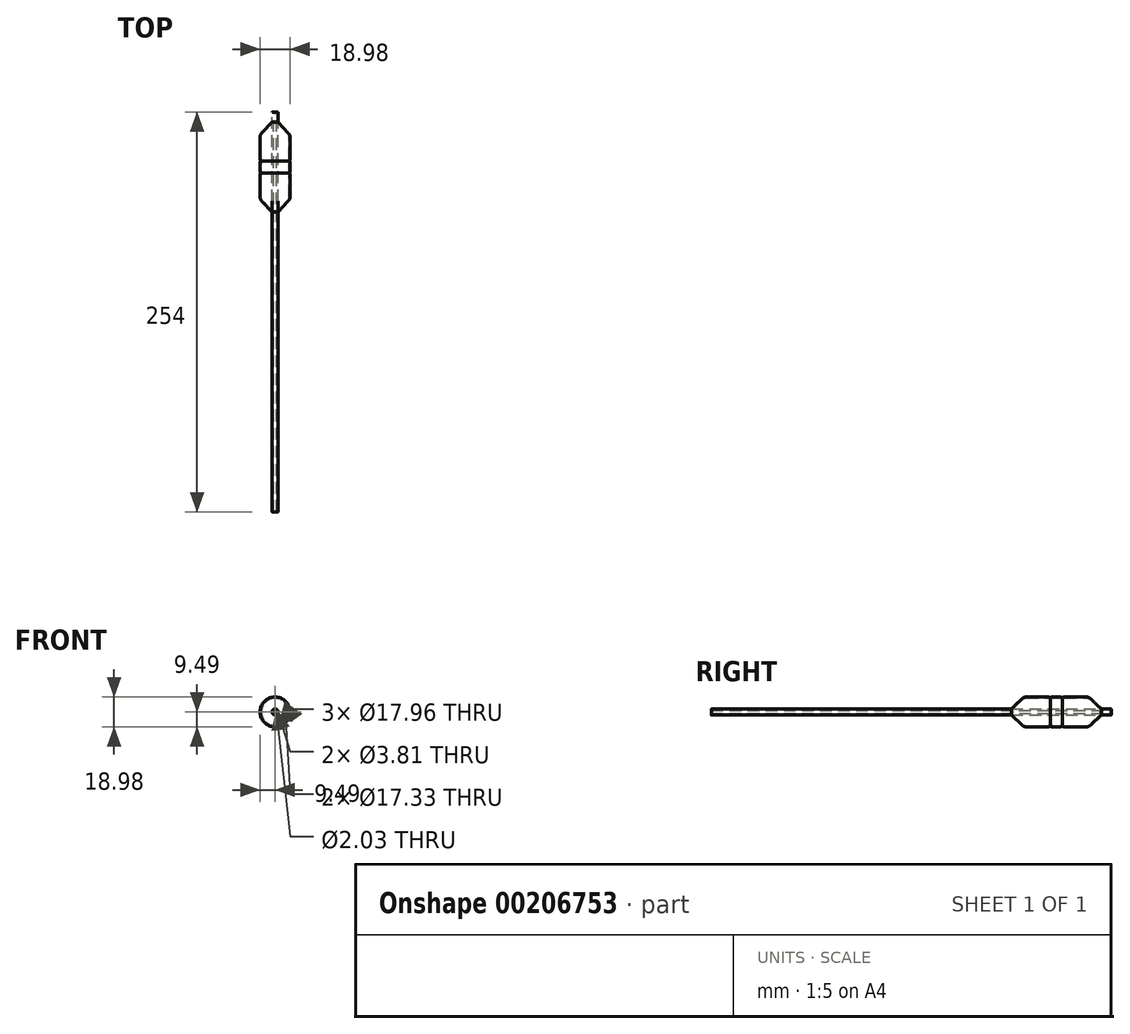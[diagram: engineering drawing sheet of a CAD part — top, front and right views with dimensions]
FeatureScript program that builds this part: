
annotation { "Feature Type Name" : "Feature", "Feature Type Description" : "" }
export const myFeature = defineFeature(function(context is Context, id is Id, definition is map)
    precondition{}
    {
        {
            var Q0;
            Q0=qCreatedBy(makeId("Front.planeOp"),FACE);
            var sketch = newSketch(context, id + "F0", { "sketchPlane" : qUnion([Q0])});
            skCircle(sketch, "E0", {"center": v(0, 0) * mm, "radius": 1.02 * mm});
            skCircle(sketch, "E1", {"center": v(0, 0) * mm, "radius": 1.9 * mm});
            skSolve(sketch);
        }
        {
            var Q0;
            Q0=makeQuery(id+"F0.imprint","IMPRINT",FACE,{"disambiguationData":[TD([[makeQuery(id+"F0.imprint","IMPRINT",EDGE,{"derivedFrom":sQuery(id+"F0.wireOp",EDGE,"E0")}),-1.0]])]});
            extrude(context, id + "F1", {"entities" : qUnion([Q0]), "depth" : 254 * mm});
        }
        {
            var Q0;
            Q0=makeQuery(id+"F1.opExtrude","CAP_EDGE",EDGE,{"disambiguationData":[OSD([sQuery(id+"F0.wireOp",EDGE,"E0")])],"isStart":true});
            chamfer(context, id + "F2", {"entities" : qUnion([Q0]), "width" : 0.56 * mm, "tangentPropagation" : true});
        }
        {
            var Q0;
            Q0=makeQuery(id+"F1.opExtrude","CAP_EDGE",EDGE,{"disambiguationData":[OSD([sQuery(id+"F0.wireOp",EDGE,"E1")])],"isStart":true});
            fillet(context, id + "F3", {"entities" : qUnion([Q0]), "radius" : 0.13 * mm, "tangentPropagation" : true, "allowEdgeOverflow" : false});
        }
        {
            var Q0;
            Q0=makeQuery(id+"F1.opExtrude","CAP_EDGE",EDGE,{"disambiguationData":[OSD([sQuery(id+"F0.wireOp",EDGE,"E1")])],"isStart":false});
            fillet(context, id + "F4", {"entities" : qUnion([Q0]), "radius" : 0.13 * mm, "tangentPropagation" : true, "allowEdgeOverflow" : false});
        }
        {
            var Q0;
            Q0=qCreatedBy(makeId("Right.planeOp"),FACE);
            var sketch = newSketch(context, id + "F5", { "sketchPlane" : qUnion([Q0])});
            skLineSegment(sketch, "E2", {"start": v(0, 0) * mm, "end": v(-318.3, 0) * mm, "construction": true});
            skSolve(sketch);
        }
        {
            var Q0;
            Q0=qCreatedBy(makeId("Right.planeOp"),FACE);
            var sketch = newSketch(context, id + "F6", { "sketchPlane" : qUnion([Q0])});
            skLineSegment(sketch, "E3.0", {"start": v(-253.87, 0) * mm, "end": v(-253.87, -1.9) * mm, "construction": true});
            skLineSegment(sketch, "E4", {"start": v(-63.45, 1.9) * mm, "end": v(-62.71, 1.9) * mm});
            skLineSegment(sketch, "E5", {"start": v(-63.45, 1.9) * mm, "end": v(-56.57, 8.44) * mm});
            skLineSegment(sketch, "E6.0", {"start": v(0, 0) * mm, "end": v(-318.3, 0) * mm, "construction": true});
            skLineSegment(sketch, "E7", {"start": v(-62.71, 1.9) * mm, "end": v(-56.37, 7.93) * mm});
            skPoint(sketch, "E8.orphan", {"position": v(-253.87, 1.9) * mm});
            skArc(sketch, "E9.filletArc", {"start": v(-53.95, 9.49) * mm, "mid": v(-55.36, 9.22) * mm, "end": v(-56.57, 8.44) * mm});
            skArc(sketch, "E10.filletArc", {"start": v(-53.75, 8.98) * mm, "mid": v(-55.16, 8.7) * mm, "end": v(-56.37, 7.93) * mm});
            skLineSegment(sketch, "E11", {"start": v(-34.9, 9.49) * mm, "end": v(-34.9, -17.87) * mm, "construction": true});
            skLineSegment(sketch, "E12", {"start": v(-53.75, 8.98) * mm, "end": v(-40.05, 8.98) * mm});
            skLineSegment(sketch, "E13", {"start": v(-40.05, 8.98) * mm, "end": v(-38.84, 8.66) * mm});
            skLineSegment(sketch, "E14", {"start": v(-38.84, 8.66) * mm, "end": v(-38.58, 8.66) * mm});
            skLineSegment(sketch, "E15", {"start": v(-38.58, 8.66) * mm, "end": v(-37.37, 8.98) * mm});
            skLineSegment(sketch, "E16", {"start": v(-37.37, 8.98) * mm, "end": v(-34.9, 8.98) * mm});
            skLineSegment(sketch, "E17", {"start": v(-53.95, 9.49) * mm, "end": v(-39.98, 9.49) * mm});
            skLineSegment(sketch, "E18", {"start": v(-39.98, 9.49) * mm, "end": v(-38.77, 9.17) * mm});
            skLineSegment(sketch, "E19", {"start": v(-38.77, 9.17) * mm, "end": v(-38.65, 9.17) * mm});
            skLineSegment(sketch, "E20", {"start": v(-38.65, 9.17) * mm, "end": v(-37.44, 9.49) * mm});
            skLineSegment(sketch, "E21", {"start": v(-37.44, 9.49) * mm, "end": v(-34.9, 9.49) * mm});
            skLineSegment(sketch, "E22.MirrorCS", {"start": v(-16.05, 8.98) * mm, "end": v(-29.75, 8.98) * mm});
            skLineSegment(sketch, "E23.MirrorCS", {"start": v(-15.85, 9.49) * mm, "end": v(-29.82, 9.49) * mm});
            skLineSegment(sketch, "E24.MirrorCS", {"start": v(-29.75, 8.98) * mm, "end": v(-30.96, 8.66) * mm});
            skLineSegment(sketch, "E25.MirrorCS", {"start": v(-29.82, 9.49) * mm, "end": v(-31.03, 9.17) * mm});
            skLineSegment(sketch, "E26.MirrorCS", {"start": v(-31.03, 9.17) * mm, "end": v(-31.15, 9.17) * mm});
            skLineSegment(sketch, "E27.MirrorCS", {"start": v(-30.96, 8.66) * mm, "end": v(-31.22, 8.66) * mm});
            skLineSegment(sketch, "E28.MirrorCS", {"start": v(-31.22, 8.66) * mm, "end": v(-32.43, 8.98) * mm});
            skLineSegment(sketch, "E29.MirrorCS", {"start": v(-31.15, 9.17) * mm, "end": v(-32.36, 9.49) * mm});
            skLineSegment(sketch, "E30.MirrorCS", {"start": v(-32.43, 8.98) * mm, "end": v(-34.9, 8.98) * mm});
            skLineSegment(sketch, "E31.MirrorCS", {"start": v(-32.36, 9.49) * mm, "end": v(-34.9, 9.49) * mm});
            skLineSegment(sketch, "E32", {"start": v(-38.7, 9.17) * mm, "end": v(-38.7, 8.66) * mm, "construction": true});
            skLineSegment(sketch, "E33.MirrorCS", {"start": v(-31.09, 9.17) * mm, "end": v(-31.09, 8.66) * mm, "construction": true});
            skArc(sketch, "E34.MirrorCS", {"start": v(-16.05, 8.98) * mm, "mid": v(-14.64, 8.7) * mm, "end": v(-13.43, 7.93) * mm});
            skArc(sketch, "E35.MirrorCS", {"start": v(-15.85, 9.49) * mm, "mid": v(-14.44, 9.22) * mm, "end": v(-13.22, 8.44) * mm});
            skLineSegment(sketch, "E36.MirrorCS", {"start": v(-7.09, 1.9) * mm, "end": v(-13.43, 7.93) * mm});
            skLineSegment(sketch, "E37.MirrorCS", {"start": v(-6.35, 1.9) * mm, "end": v(-13.22, 8.44) * mm});
            skLineSegment(sketch, "E38.MirrorCS", {"start": v(-6.35, 1.9) * mm, "end": v(-7.09, 1.9) * mm});
            skSolve(sketch);
        }
        {
            var Q0;
            Q0=qSketchRegion(id+"F6",true);
            var Q1;
            Q1=sQuery(id+"F6.wireOp",EDGE,"E6.0");
            revolve(context, id + "F7", {"entities" : qUnion([Q0]), "axis" : qUnion([Q1]), "revolveType" : RevolveType.FULL});
        }
        {
            var Q0;
            Q0=makeQuery(id+"F7.opRevolve","SWEPT_EDGE",EDGE,{"disambiguationData":[OSD([sQuery(id+"F6.wireOp",EDGE,"E17"),sQuery(id+"F6.wireOp",EDGE,"E18")])]});
            var Q1;
            Q1=makeQuery(id+"F7.opRevolve","SWEPT_EDGE",EDGE,{"disambiguationData":[OSD([sQuery(id+"F6.wireOp",EDGE,"E20"),sQuery(id+"F6.wireOp",EDGE,"E21")])]});
            var Q2;
            Q2=makeQuery(id+"F7.opRevolve","SWEPT_EDGE",EDGE,{"disambiguationData":[OSD([sQuery(id+"F6.wireOp",EDGE,"E29.MirrorCS"),sQuery(id+"F6.wireOp",EDGE,"E31.MirrorCS")])]});
            var Q3;
            Q3=makeQuery(id+"F7.opRevolve","SWEPT_EDGE",EDGE,{"disambiguationData":[OSD([sQuery(id+"F6.wireOp",EDGE,"E23.MirrorCS"),sQuery(id+"F6.wireOp",EDGE,"E25.MirrorCS")])]});
            var Q4;
            Q4=makeQuery(id+"F7.opRevolve","SWEPT_EDGE",EDGE,{"disambiguationData":[OSD([sQuery(id+"F6.wireOp",EDGE,"E22.MirrorCS"),sQuery(id+"F6.wireOp",EDGE,"E24.MirrorCS")])]});
            var Q5;
            Q5=makeQuery(id+"F7.opRevolve","SWEPT_EDGE",EDGE,{"disambiguationData":[OSD([sQuery(id+"F6.wireOp",EDGE,"E28.MirrorCS"),sQuery(id+"F6.wireOp",EDGE,"E30.MirrorCS")])]});
            var Q6;
            Q6=makeQuery(id+"F7.opRevolve","SWEPT_EDGE",EDGE,{"disambiguationData":[OSD([sQuery(id+"F6.wireOp",EDGE,"E15"),sQuery(id+"F6.wireOp",EDGE,"E16")])]});
            var Q7;
            Q7=makeQuery(id+"F7.opRevolve","SWEPT_EDGE",EDGE,{"disambiguationData":[OSD([sQuery(id+"F6.wireOp",EDGE,"E12"),sQuery(id+"F6.wireOp",EDGE,"E13")])]});
            fillet(context, id + "F8", {"entities" : qUnion([Q0, Q1, Q2, Q3, Q4, Q5, Q6, Q7]), "radius" : 1.27 * mm, "tangentPropagation" : true, "allowEdgeOverflow" : false});
        }
    });
